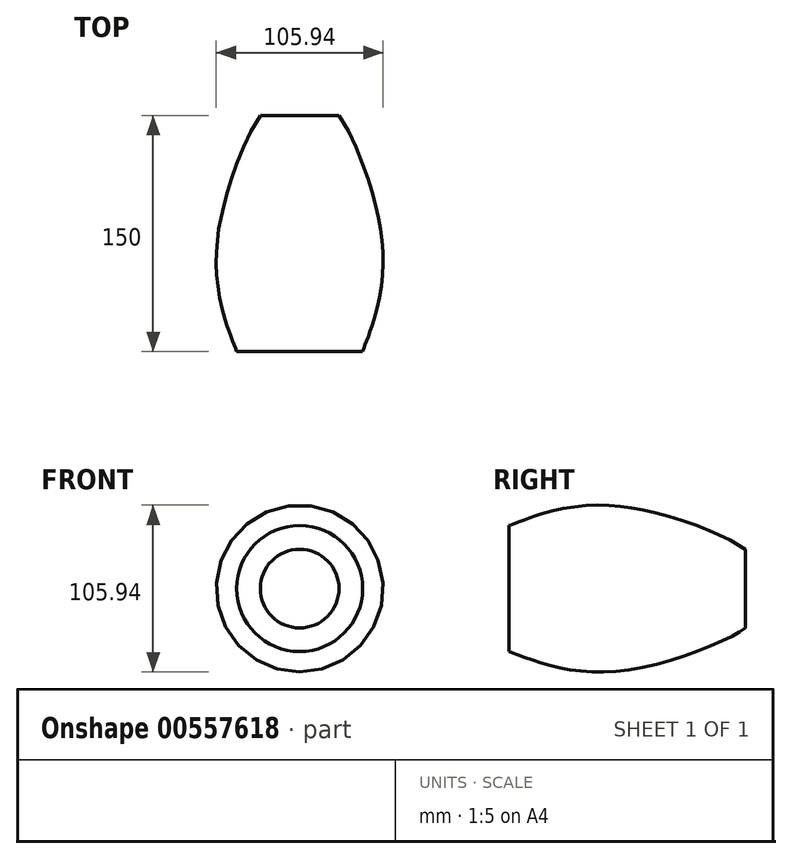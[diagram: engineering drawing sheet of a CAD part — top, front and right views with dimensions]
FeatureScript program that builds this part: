
annotation { "Feature Type Name" : "Feature", "Feature Type Description" : "" }
export const myFeature = defineFeature(function(context is Context, id is Id, definition is map)
    precondition{}
    {
        {
            var Q0;
            Q0=qCreatedBy(makeId("Front.planeOp"),FACE);
            var sketch = newSketch(context, id + "F0", { "sketchPlane" : qUnion([Q0])});
            skCircle(sketch, "E0", {"center": v(0, 0) * mm, "radius": 25 * mm});
            skCircle(sketch, "E1", {"center": v(0, 0) * mm, "radius": 21 * mm});
            skCircle(sketch, "E2", {"center": v(0, 0) * mm, "radius": 40 * mm});
            skSolve(sketch);
        }
        {
            var Q0;
            Q0=qCreatedBy(makeId("Right.planeOp"),FACE);
            var sketch = newSketch(context, id + "F1", { "sketchPlane" : qUnion([Q0])});
            skFitSpline(sketch, "E3", {"points": [v(0, 25) * mm, v(-67.72, 50.61) * mm, v(-128.43, 47.64) * mm, v(-150, 40) * mm], "startDerivative": vector(-63.98, 52.3) * mm, "endDerivative": vector(-38.57, -10.61) * mm});
            skSolve(sketch);
        }
        {
            var Q0;
            Q0=qCreatedBy(makeId("Front.planeOp"),FACE);
            cPlane(context, id + "F2", {"entities" : qUnion([Q0]), "cplaneType" : CPlaneType.OFFSET, "offset" : 150 * mm, "width" : 150 * mm, "height" : 150 * mm});
        }
        {
            var Q0;
            Q0=qCreatedBy(makeId("Top.planeOp"),FACE);
            var sketch = newSketch(context, id + "F3", { "sketchPlane" : qUnion([Q0])});
            skLineSegment(sketch, "E4", {"start": v(-24.8, 0) * mm, "end": v(-40.86, -147.15) * mm});
            skLineSegment(sketch, "E5", {"start": v(-40.86, -147.15) * mm, "end": v(39.14, -150.08) * mm});
            skLineSegment(sketch, "E6", {"start": v(39.14, -150.08) * mm, "end": v(25.2, 0) * mm});
            skLineSegment(sketch, "E7", {"start": v(25.2, 0) * mm, "end": v(-24.8, 0) * mm});
            skLineSegment(sketch, "E8", {"start": v(0, 0) * mm, "end": v(0, -148.65) * mm});
            skSolve(sketch);
        }
        {
            var Q0;
            Q0=sQuery(id+"F1.wireOp",EDGE,"E3");
            var Q1;
            Q1=sQuery(id+"F3.wireOp",EDGE,"E8");
            revolve(context, id + "F4", {"bodyType" : ToolBodyType.SURFACE, "surfaceEntities" : qUnion([Q0]), "axis" : qUnion([Q1]), "revolveType" : RevolveType.FULL});
        }
    });
